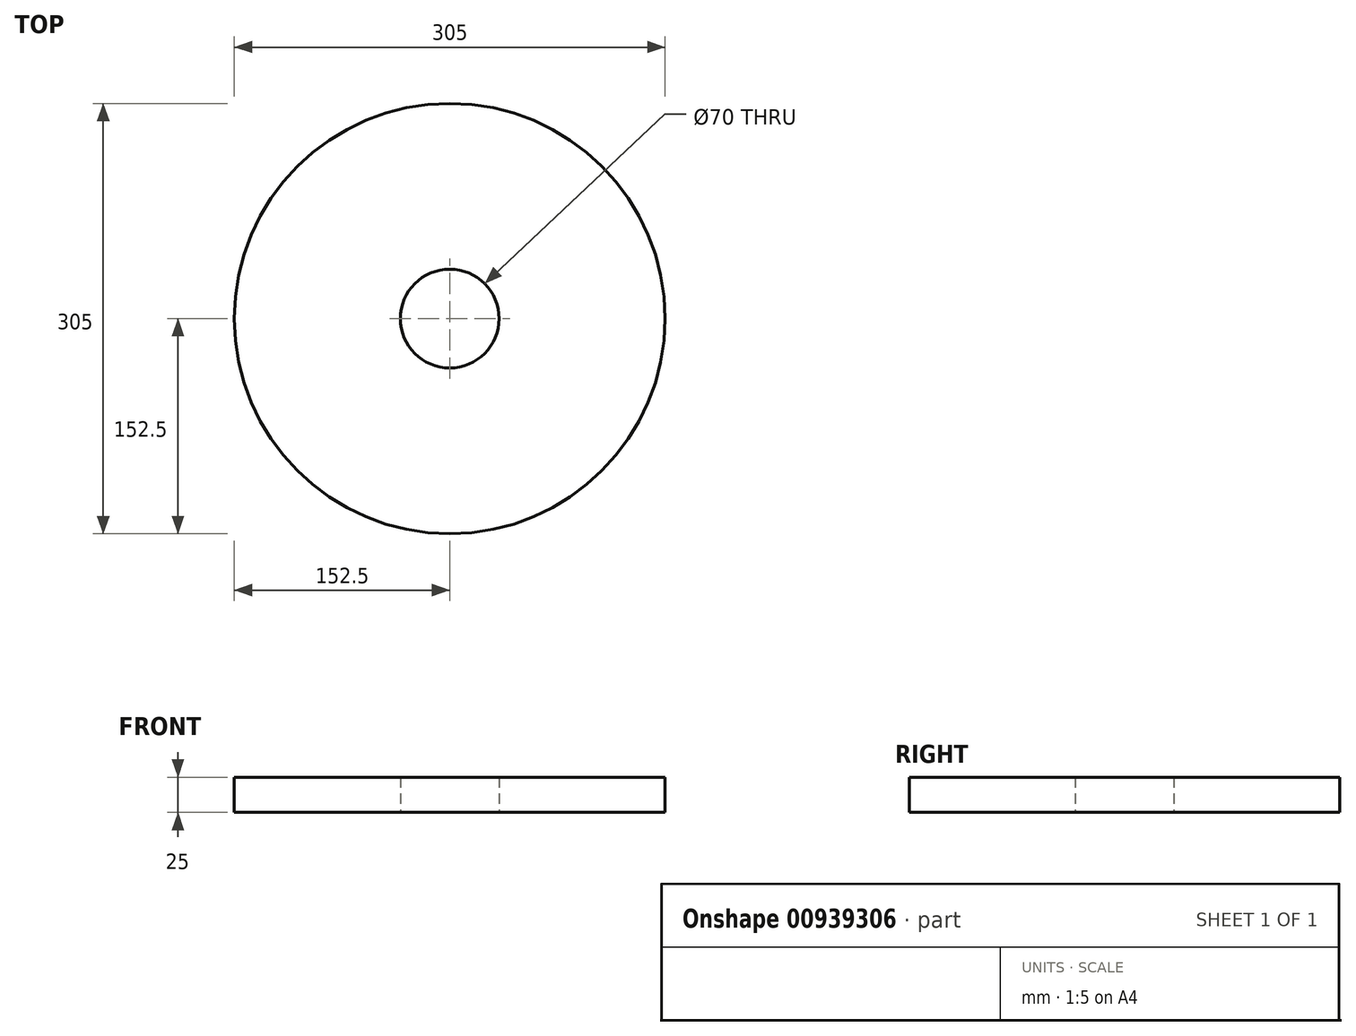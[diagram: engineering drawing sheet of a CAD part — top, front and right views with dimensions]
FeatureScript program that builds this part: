
annotation { "Feature Type Name" : "Feature", "Feature Type Description" : "" }
export const myFeature = defineFeature(function(context is Context, id is Id, definition is map)
    precondition{}
    {
        {
            var Q0;
            Q0=qCreatedBy(makeId("Top.planeOp"),FACE);
            var sketch = newSketch(context, id + "F0", { "sketchPlane" : qUnion([Q0])});
            skCircle(sketch, "E0", {"center": v(0, 0) * mm, "radius": 152.5 * mm});
            skCircle(sketch, "E1", {"center": v(0, 0) * mm, "radius": 35 * mm});
            skSolve(sketch);
        }
        {
            var Q0;
            Q0 = qSketchRegion(id + "F0", true);
            extrude(context, id + "F1", {"entities" : qUnion([Q0]), "depth" : 25 * mm, "offsetDistance" : 25 * mm});
        }
    });
